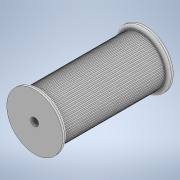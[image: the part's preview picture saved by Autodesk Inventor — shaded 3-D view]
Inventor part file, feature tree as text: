
AUTODESK INVENTOR PART (.ipt)
format: ipt  version: 2020 (Build 240168000, 168)  size: 283,136 bytes
history: native  units: in
note: dims shown in document units (in); Inventor stores cm internally (conversion verified against a paired STEP export)
features: sketch x2, revolve x1, fillet x1, extrude x1, pattern_circular x1
ambient origin geometry x8: Origin, YZ Plane, XZ Plane, XY Plane, X Axis, Y Axis, Z Axis, Center Point
bodies: Solid1 (feature_tree)
feature tree (6):
  revolve  "Revolution1"  [1 undecoded]
  fillet  "Fillet1"  Radius=4.1339in
  extrude  "Extrusion1"  Depth=0.1969in
  pattern_circular  "Circular Pattern1"  [2 undecoded]
  sketch  "Sketch1"  dims[d0=0.9843in d1=0.1969in d2=4.1339in]
  sketch  "Sketch2"  dims[d4=0.1575in d5=0.1969in d6=0.1594in d8=0.1594in d9=90.0deg d10=0.1181in d11=0.0591in d12=4.1339in d13=0.0in d14=23.622in d15=360.0deg d18=4.1339in]
note: 3 required parameter values undecoded (feature->parameter linkage not recoverable at this tier; creation-order binding heuristic only, values carry confidence <= 0.55)